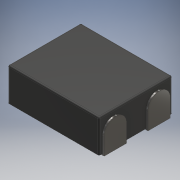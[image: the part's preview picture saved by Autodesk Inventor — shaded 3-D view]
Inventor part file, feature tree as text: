
AUTODESK INVENTOR PART (.ipt)
format: ipt  version: 2018 (Build 220112000, 112)  size: 149,504 bytes
history: native  units: mm
features: other x6, plane x3, extrude x2, sketch x2, mirror x1, fillet x1
ambient origin geometry x8: Origin, YZ Plane, XZ Plane, XY Plane, X Axis, Y Axis, Z Axis, Center Point
bodies: Body1 (feature_tree), Body2 (feature_tree), Body3 (feature_tree)
feature tree (15):
  other  "Sólido1"
  extrude  "Extrusión1"  Depth=1.0mm
  plane  "Plano de trabajo1"
  extrude  "Extrusión2"  TaperAngle=90.0deg  [1 undecoded]
  other  "Edición directa1"
  plane  "Plano de trabajo3"
  mirror  "Simetría1"
  fillet  "Empalme1"  Radius=0.3mm
  sketch  "Boceto1"  dims[d0=1.25mm d1=1.0mm]
  sketch  "Boceto2"  dims[d2=0.45mm d3=0.0mm d4=90.0deg d5=0.3mm d6=0.0mm d7=0.0mm d8=-0.02mm d9=-0.02mm d10=90.0deg d11=0.02mm]
  other  "Sólido2"
  plane  "Plano de trabajo2"
  other  "Patrón de Sólido2:1"
  other  "Sólido3"
  other  "Desplazar1"
note: 1 required parameter value undecoded (feature->parameter linkage not recoverable at this tier; creation-order binding heuristic only, values carry confidence <= 0.55)
